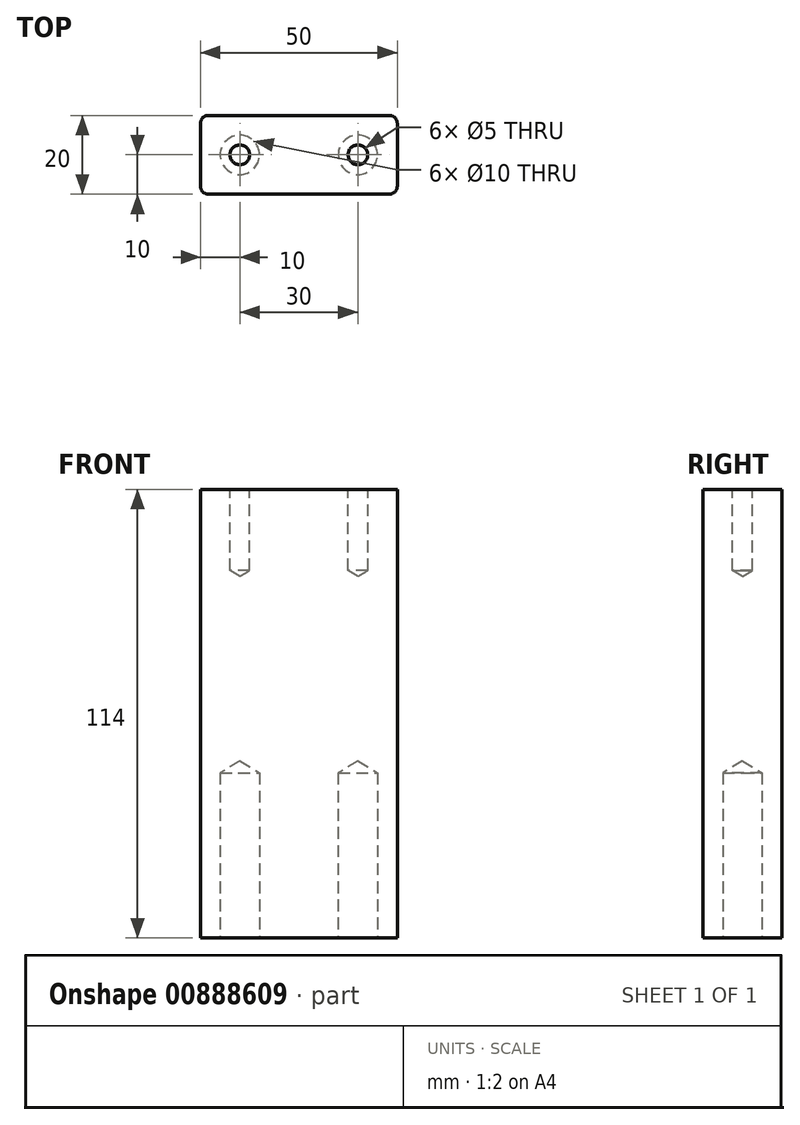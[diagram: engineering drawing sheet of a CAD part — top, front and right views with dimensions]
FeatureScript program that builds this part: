
annotation { "Feature Type Name" : "Feature", "Feature Type Description" : "" }
export const myFeature = defineFeature(function(context is Context, id is Id, definition is map)
    precondition{}
    {
        {
            var Q0;
            Q0=qCreatedBy(makeId("Top.planeOp"),FACE);
            var sketch = newSketch(context, id + "F0", { "sketchPlane" : qUnion([Q0])});
            skLineSegment(sketch, "E0.bottom", {"start": v(25, 10) * mm, "end": v(-25, 10) * mm});
            skLineSegment(sketch, "E0.top", {"start": v(25, -10) * mm, "end": v(-25, -10) * mm});
            skLineSegment(sketch, "E0.left", {"start": v(25, 10) * mm, "end": v(25, -10) * mm});
            skLineSegment(sketch, "E0.right", {"start": v(-25, 10) * mm, "end": v(-25, -10) * mm});
            skPoint(sketch, "E0.middle", {"position": v(0, 0) * mm});
            skSolve(sketch);
        }
        {
            var Q0;
            Q0=makeQuery(id+"F0.imprint","IMPRINT",FACE,{"disambiguationData":[TD([[makeQuery(id+"F0.imprint","IMPRINT",EDGE,{"derivedFrom":sQuery(id+"F0.wireOp",EDGE,"E0.bottom")}),1.0]])]});
            extrude(context, id + "F1", {"entities" : qUnion([Q0]), "depth" : 114 * mm, "offsetDistance" : 25 * mm});
        }
        {
            var Q0;
            Q0=makeQuery(id+"F1.opExtrude","CAP_FACE",FACE,{"disambiguationData":[OSD([sQuery(id+"F0.wireOp",EDGE,"E0.bottom"),sQuery(id+"F0.wireOp",EDGE,"E0.top"),sQuery(id+"F0.wireOp",EDGE,"E0.left"),sQuery(id+"F0.wireOp",EDGE,"E0.right")])],"isStart":false});
            var sketch = newSketch(context, id + "F2", { "sketchPlane" : qUnion([Q0])});
            skLineSegment(sketch, "E1", {"start": v(-25, 0) * mm, "end": v(25, 0) * mm, "construction": true});
            skCircle(sketch, "E2", {"center": v(-15, 0) * mm, "radius": 3 * mm});
            skCircle(sketch, "E3", {"center": v(15, 0) * mm, "radius": 3 * mm});
            skSolve(sketch);
        }
        {
            var Q0;
            Q0=sQuery(id+"F2.wireOp",VERTEX,"E2.center");
            var Q1;
            Q1=sQuery(id+"F2.wireOp",VERTEX,"E3.center");
            var Q2;
            Q2=makeQuery(id+"F1.opExtrude","SWEPT_BODY",BODY,{"disambiguationData":[OSD([sQuery(id+"F0.wireOp",EDGE,"E0.bottom"),sQuery(id+"F0.wireOp",EDGE,"E0.top"),sQuery(id+"F0.wireOp",EDGE,"E0.left"),sQuery(id+"F0.wireOp",EDGE,"E0.right")])]});
            hole(context, id + "F3", {"style" : HoleStyle.SIMPLE, "endStyle" : HoleEndStyle.BLIND, "standardTappedOrClearance" : lookupTablePath({ "standard" : "ISO", "engagement" : "75%", "pitch" : "1 mm", "size" : "M6", "type" : "Tapped" }), "standardBlindInLast" : lookupTablePath({ "standard" : "ISO", "engagement" : "75%", "pitch" : "1 mm", "size" : "M6", "type" : "Tapped" }), "holeDiameter" : 5 * mm, "majorDiameter" : 6 * mm, "showTappedDepth" : true, "holeDepth" : 20.6 * mm, "tappedDepth" : 17.6 * mm, "tapClearance" : 3, "locations" : qUnion([Q0, Q1]), "scope" : qUnion([Q2])});
        }
        {
            var Q0;
            Q0=makeQuery(id+"F1.opExtrude","CAP_FACE",FACE,{"disambiguationData":[OSD([sQuery(id+"F0.wireOp",EDGE,"E0.bottom"),sQuery(id+"F0.wireOp",EDGE,"E0.top"),sQuery(id+"F0.wireOp",EDGE,"E0.left"),sQuery(id+"F0.wireOp",EDGE,"E0.right")])],"isStart":true});
            var sketch = newSketch(context, id + "F4", { "sketchPlane" : qUnion([Q0])});
            skCircle(sketch, "E4", {"center": v(-15, 0) * mm, "radius": 5 * mm});
            skCircle(sketch, "E5.MirrorC", {"center": v(15, 0) * mm, "radius": 5 * mm});
            skSolve(sketch);
        }
        {
            var Q0;
            Q0=sQuery(id+"F4.wireOp",VERTEX,"E4.center");
            var Q1;
            Q1=sQuery(id+"F4.wireOp",VERTEX,"E5.MirrorC.center");
            var Q2;
            Q2=makeQuery(id+"F1.opExtrude","SWEPT_BODY",BODY,{"disambiguationData":[OSD([sQuery(id+"F0.wireOp",EDGE,"E0.bottom"),sQuery(id+"F0.wireOp",EDGE,"E0.top"),sQuery(id+"F0.wireOp",EDGE,"E0.left"),sQuery(id+"F0.wireOp",EDGE,"E0.right")])]});
            hole(context, id + "F5", {"style" : HoleStyle.SIMPLE, "endStyle" : HoleEndStyle.BLIND, "holeDiameter" : 10 * mm, "majorDiameter" : 5 * mm, "holeDepth" : 42 * mm, "tappedDepth" : 17.6 * mm, "tapClearance" : 3, "locations" : qUnion([Q0, Q1]), "scope" : qUnion([Q2])});
        }
        {
            var Q0;
            Q0=makeQuery(id+"F1.opExtrude","SWEPT_EDGE",EDGE,{"disambiguationData":[OSD([sQuery(id+"F0.wireOp",EDGE,"E0.top"),sQuery(id+"F0.wireOp",EDGE,"E0.left")])]});
            var Q1;
            Q1=makeQuery(id+"F1.opExtrude","SWEPT_EDGE",EDGE,{"disambiguationData":[OSD([sQuery(id+"F0.wireOp",EDGE,"E0.top"),sQuery(id+"F0.wireOp",EDGE,"E0.right")])]});
            var Q2;
            Q2=makeQuery(id+"F1.opExtrude","SWEPT_EDGE",EDGE,{"disambiguationData":[OSD([sQuery(id+"F0.wireOp",EDGE,"E0.bottom"),sQuery(id+"F0.wireOp",EDGE,"E0.right")])]});
            var Q3;
            Q3=makeQuery(id+"F1.opExtrude","SWEPT_EDGE",EDGE,{"disambiguationData":[OSD([sQuery(id+"F0.wireOp",EDGE,"E0.bottom"),sQuery(id+"F0.wireOp",EDGE,"E0.left")])]});
            fillet(context, id + "F6", {"entities" : qUnion([Q0, Q1, Q2, Q3]), "radius" : 2 * mm, "tangentPropagation" : true, "allowEdgeOverflow" : false});
        }
    });
